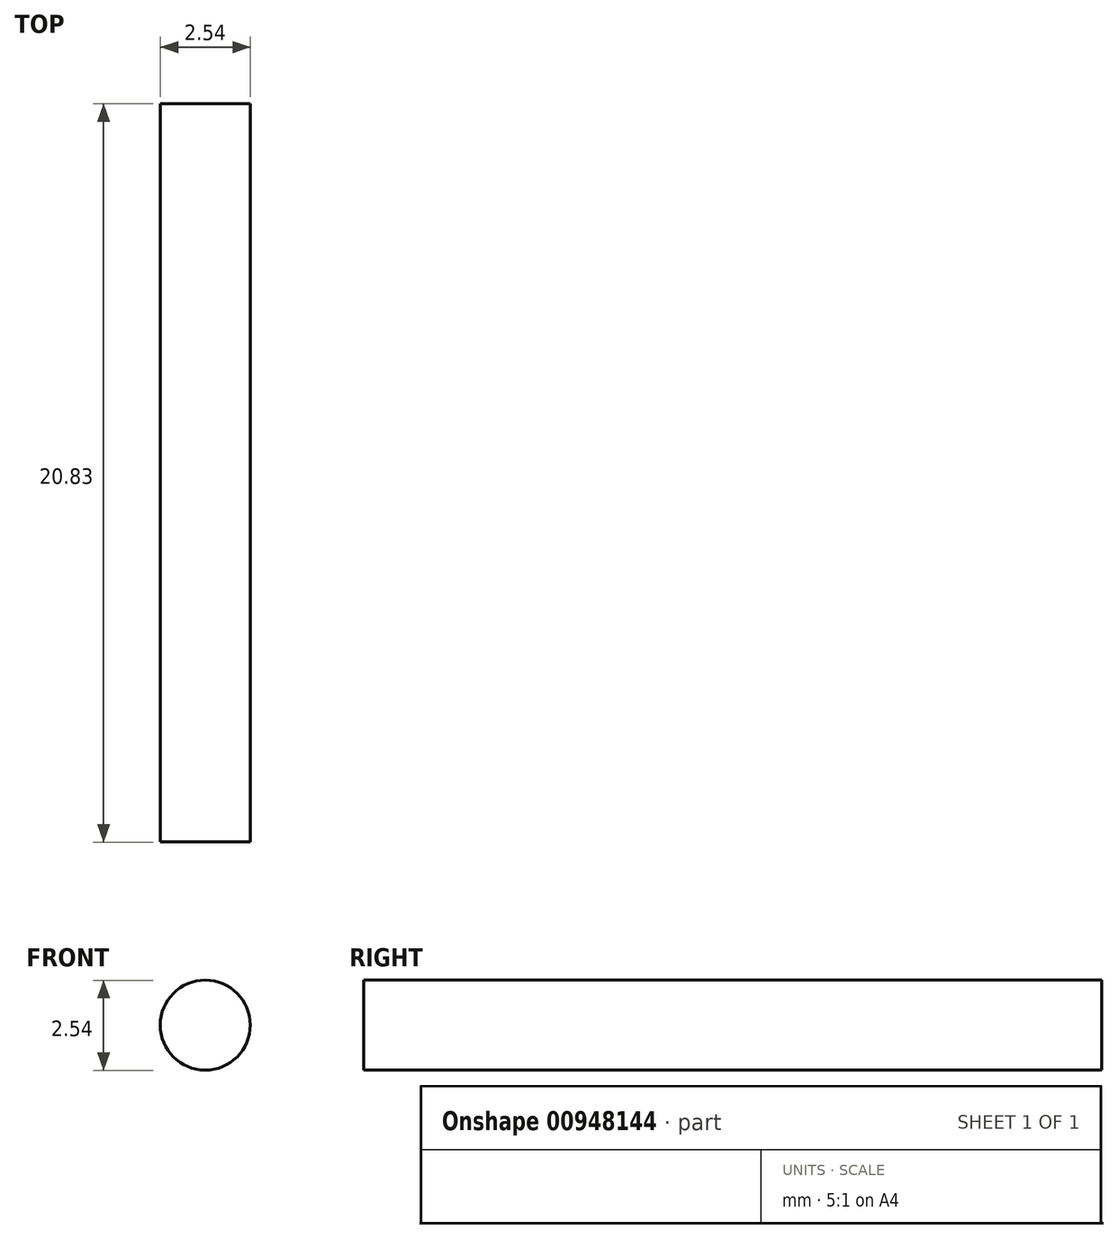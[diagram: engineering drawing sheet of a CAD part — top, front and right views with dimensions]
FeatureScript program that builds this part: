
annotation { "Feature Type Name" : "Feature", "Feature Type Description" : "" }
export const myFeature = defineFeature(function(context is Context, id is Id, definition is map)
    precondition{}
    {
        {
            var Q0;
            Q0=qCreatedBy(makeId("Front.planeOp"),FACE);
            var sketch = newSketch(context, id + "F0", { "sketchPlane" : qUnion([Q0])});
            skCircle(sketch, "E0", {"center": v(-41.58, 25.5) * mm, "radius": 1.27 * mm});
            skSolve(sketch);
        }
        {
            var Q0;
            Q0=makeQuery(id+"F0.imprint","IMPRINT",FACE,{"disambiguationData":[TD([[makeQuery(id+"F0.imprint","IMPRINT",EDGE,{"derivedFrom":sQuery(id+"F0.wireOp",EDGE,"E0")}),1.0]])]});
            extrude(context, id + "F1", {"entities" : qUnion([Q0]), "depth" : 20.83 * mm, "offsetDistance" : 25.4 * mm});
        }
    });
